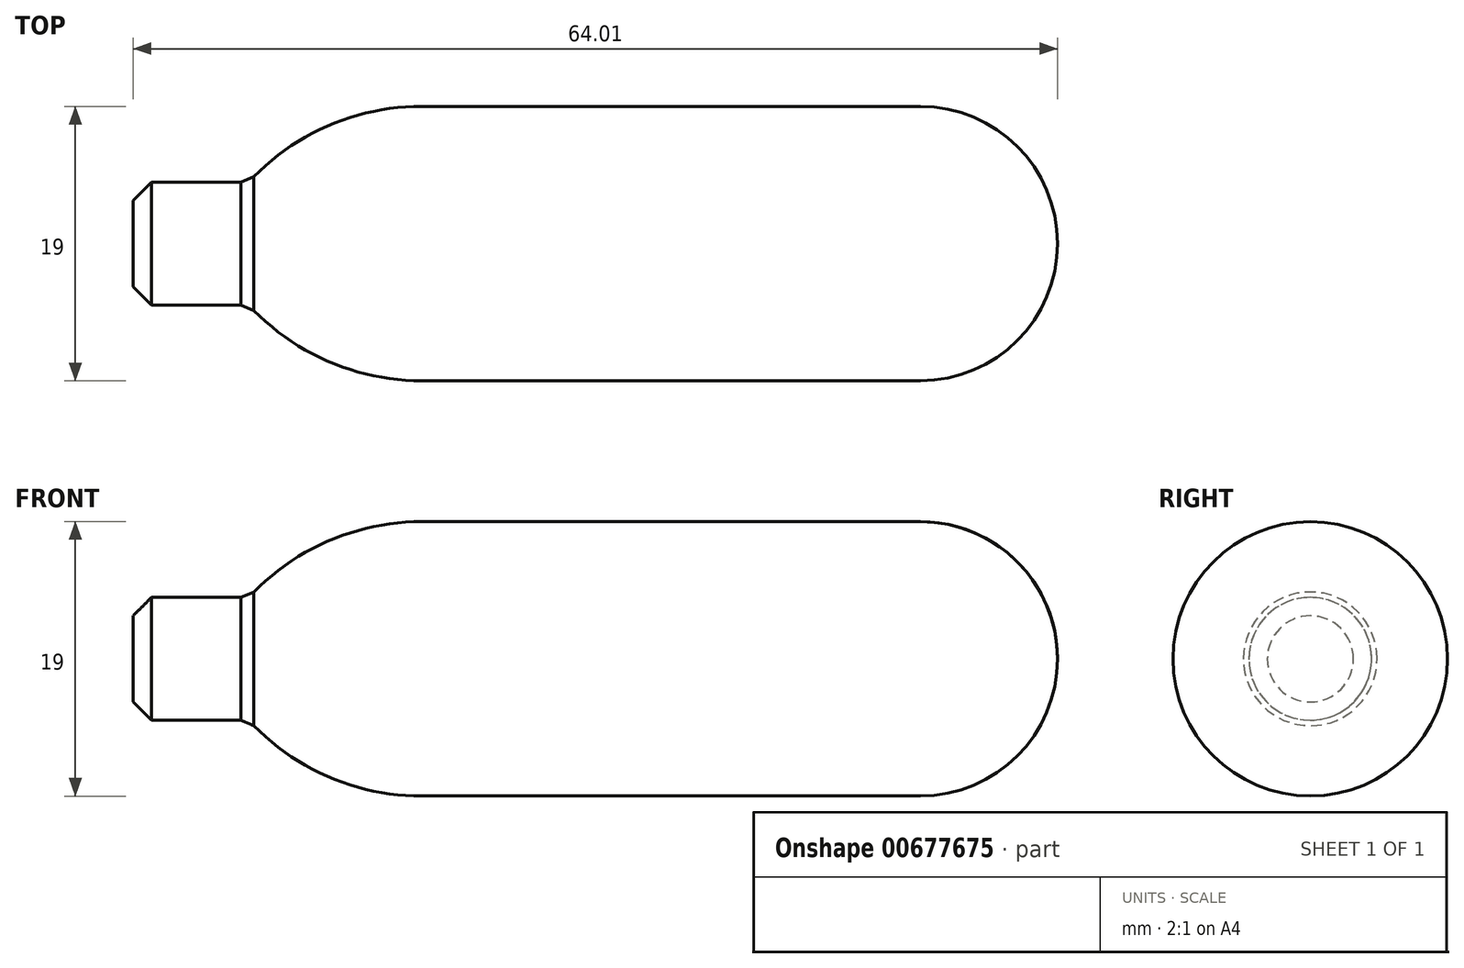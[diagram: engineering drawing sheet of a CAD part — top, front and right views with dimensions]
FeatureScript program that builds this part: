
annotation { "Feature Type Name" : "Feature", "Feature Type Description" : "" }
export const myFeature = defineFeature(function(context is Context, id is Id, definition is map)
    precondition{}
    {
        {
            var Q0;
            Q0=qCreatedBy(makeId("Front.planeOp"),FACE);
            var sketch = newSketch(context, id + "F0", { "sketchPlane" : qUnion([Q0])});
            skLineSegment(sketch, "E0", {"start": v(0, 0) * mm, "end": v(0, 4.25) * mm});
            skLineSegment(sketch, "E1", {"start": v(0, 4.25) * mm, "end": v(8, 4.25) * mm});
            skLineSegment(sketch, "E2", {"start": v(0, 0) * mm, "end": v(64, 0) * mm});
            skLineSegment(sketch, "E3", {"start": v(32, 9.5) * mm, "end": v(54.5, 9.5) * mm});
            skLineSegment(sketch, "E4", {"start": v(64, 0) * mm, "end": v(64, 0) * mm});
            skPoint(sketch, "E5", {"position": v(32, 0) * mm});
            skPoint(sketch, "E6.visualSharp", {"position": v(64, 9.5) * mm});
            skArc(sketch, "E6.filletArc", {"start": v(64, 0) * mm, "mid": v(61.23, 6.72) * mm, "end": v(54.5, 9.5) * mm});
            skPoint(sketch, "E7", {"position": v(20, 9.5) * mm});
            skLineSegment(sketch, "E8", {"start": v(32, 9.5) * mm, "end": v(20, 9.5) * mm});
            skArc(sketch, "E9", {"start": v(20, 9.5) * mm, "mid": v(13.45, 8.13) * mm, "end": v(8, 4.25) * mm});
            skLineSegment(sketch, "E10", {"start": v(0, 4.25) * mm, "end": v(0, 3.74) * mm});
            skSolve(sketch);
        }
        {
            var Q0;
            Q0=makeQuery(id+"F0.imprint","IMPRINT",FACE,{"disambiguationData":[TD([[makeQuery(id+"F0.imprint","IMPRINT",EDGE,{"derivedFrom":sQuery(id+"F0.wireOp",EDGE,"E0")}),-1.0]])]});
            var Q1;
            Q1=sQuery(id+"F0.wireOp",EDGE,"E2");
            revolve(context, id + "F1", {"entities" : qUnion([Q0]), "axis" : qUnion([Q1]), "revolveType" : RevolveType.ONE_DIRECTION, "angle" : 360 * degree});
        }
        {
            var Q0;
            Q0=makeQuery(id+"F1.opRevolve","SWEPT_EDGE",EDGE,{"disambiguationData":[OSD([sQuery(id+"F0.wireOp",EDGE,"E1"),sQuery(id+"F0.wireOp",EDGE,"E10")])]});
            chamfer(context, id + "F2", {"entities" : qUnion([Q0]), "width" : 1.27 * mm, "tangentPropagation" : true});
        }
    });
